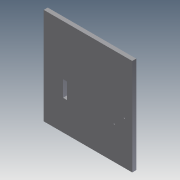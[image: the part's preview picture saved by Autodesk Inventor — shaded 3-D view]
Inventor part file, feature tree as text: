
AUTODESK INVENTOR PART (.ipt)
format: ipt  version: 2011 (Build 150239000, 239)  size: 246,272 bytes
history: native  units: in
note: dims shown in document units (in); Inventor stores cm internally (conversion verified against a paired STEP export)
features: extrude x21, sketch x21
ambient origin geometry x8: Origin, YZ Plane, XZ Plane, XY Plane, X Axis, Y Axis, Z Axis, Center Point
bodies: Solid1 (feature_tree)
feature tree (42):
  extrude  "Extrusion1"  Depth=5.0in
  extrude  "Extrusion2"  Depth=2.0in
  extrude  "Extrusion3"  Depth=0.25in
  extrude  "Extrusion4"  Depth=1.2598in
  extrude  "Extrusion5"  Depth=0.5in TaperAngle=0.0deg
  extrude  "Extrusion6"  Depth=0.9055in
  extrude  "Extrusion7"  Depth=0.25in
  extrude  "Extrusion8"  Depth=0.5in TaperAngle=0.0deg
  extrude  "Extrusion9"  Depth=0.25in TaperAngle=0.0deg
  extrude  "Extrusion10"  Depth=0.25in TaperAngle=0.0deg
  extrude  "Extrusion11"  Depth=0.25in TaperAngle=0.0deg
  extrude  "Extrusion12"  Depth=0.315in
  extrude  "Extrusion13"  Depth=0.6299in
  extrude  "Extrusion14"  Depth=0.0787in
  extrude  "Extrusion15"  Depth=0.3in TaperAngle=0.0deg
  extrude  "Extrusion16"  Depth=0.1299in
  extrude  "Extrusion17"  Depth=0.1299in
  extrude  "Extrusion18"  Depth=0.05in TaperAngle=0.0deg
  extrude  "Extrusion19"  Depth=0.25in
  extrude  "Extrusion20"  Depth=7.0in TaperAngle=0.0deg
  extrude  "Extrusion21"  Depth=1.0in
  sketch  "Sketch1"  dims[d0=5.0in d1=5.0in]
  sketch  "Sketch2"  dims[d2=0.25in d3=0.0in d4=2.0in]
  sketch  "Sketch3"  dims[d5=0.9055in d6=0.25in]
  sketch  "Sketch4"  dims[d7=1.5748in d8=1.2598in]
  sketch  "Sketch5"  dims[d9=0.25in d10=0.0in d11=0.5in d12=0.0in]
  sketch  "Sketch6"  dims[d13=0.5in d14=0.0in d15=0.9055in]
  sketch  "Sketch7"  dims[d16=0.25in d17=0.25in]
  sketch  "Sketch8"  dims[d18=1.0in d19=0.5in d20=0.0in]
  sketch  "Sketch9"  dims[d21=0.5in d22=0.0in d23=0.25in d24=0.0in]
  sketch  "Sketch10"  dims[d25=4.2795in d26=0.25in d27=0.0in]
  sketch  "Sketch11"  dims[d28=0.25in d29=0.25in d30=0.0in]
  sketch  "Sketch12"  dims[d31=0.4724in d32=0.315in]
  sketch  "Sketch13"  dims[d33=0.6299in d34=0.6299in]
  sketch  "Sketch14"  dims[d35=0.0787in d36=0.0787in]
  sketch  "Sketch15"  dims[d37=0.25in d38=0.0in d39=0.3in d40=0.0in]
  sketch  "Sketch16"  dims[d41=0.3in d42=0.0in d43=0.1299in]
  sketch  "Sketch17"  dims[d44=0.3in d45=0.0in d46=0.1299in]
  sketch  "Sketch18"  dims[d47=0.3in d48=0.0in d49=0.05in d50=0.0in]
  sketch  "Sketch19"  dims[d51=1.0in d52=0.0in d53=0.25in]
  sketch  "Sketch20"  dims[d54=0.25in d55=7.0in d56=0.0in]
  sketch  "Sketch21"  dims[d57=1.0in d58=1.0in d59=1.0in d60=0.0in d61=2.75in d62=1.0in d63=1.0in d64=0.0in d65=0.25in d66=0.0in d67=0.5in d68=0.0in]
